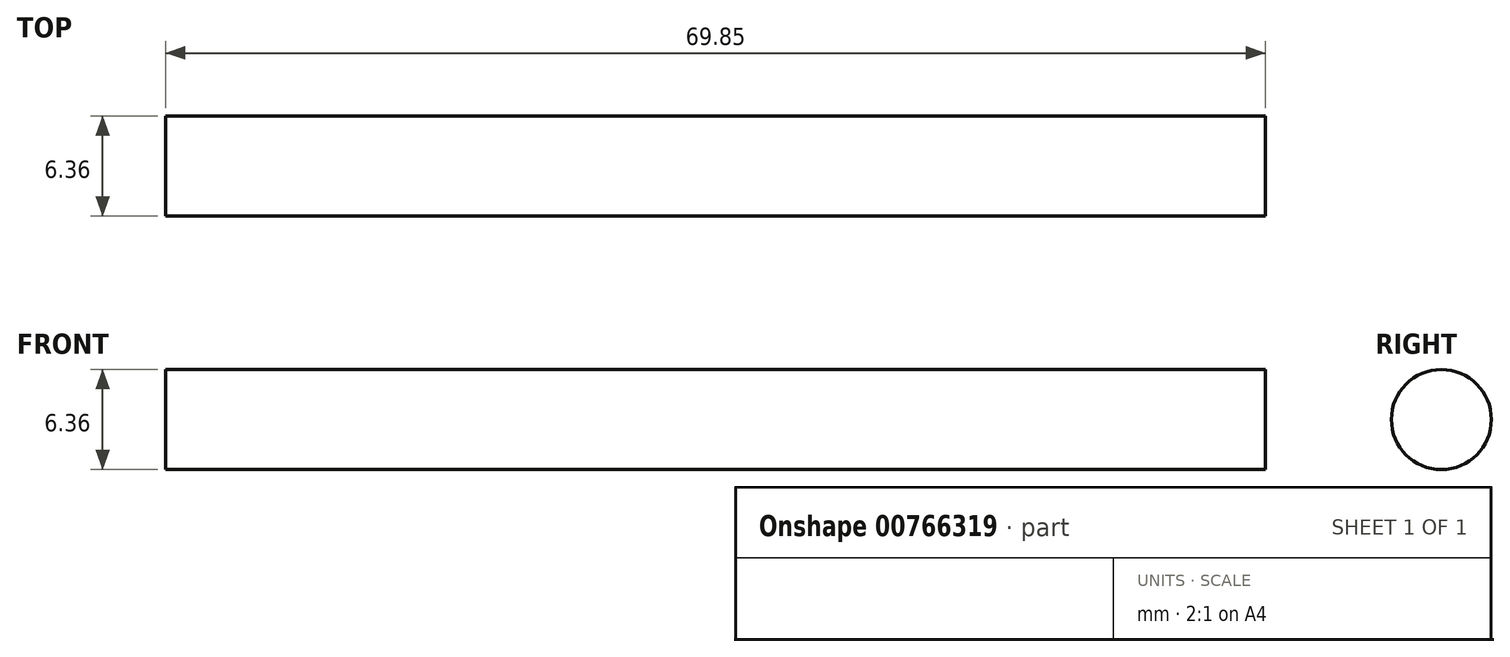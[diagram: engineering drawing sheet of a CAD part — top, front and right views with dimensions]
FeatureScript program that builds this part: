
annotation { "Feature Type Name" : "Feature", "Feature Type Description" : "" }
export const myFeature = defineFeature(function(context is Context, id is Id, definition is map)
    precondition{}
    {
        {
            var Q0;
            Q0=qCreatedBy(makeId("Right.planeOp"),FACE);
            var sketch = newSketch(context, id + "F0", { "sketchPlane" : qUnion([Q0])});
            skCircle(sketch, "E0", {"center": v(0, 0) * mm, "radius": 3.18 * mm});
            skSolve(sketch);
        }
        {
            var Q0;
            Q0 = qSketchRegion(id + "F0", true);
            extrude(context, id + "F1", {"entities" : qUnion([Q0]), "oppositeDirection" : true, "depth" : 69.85 * mm, "offsetDistance" : 25.4 * mm});
        }
    });
